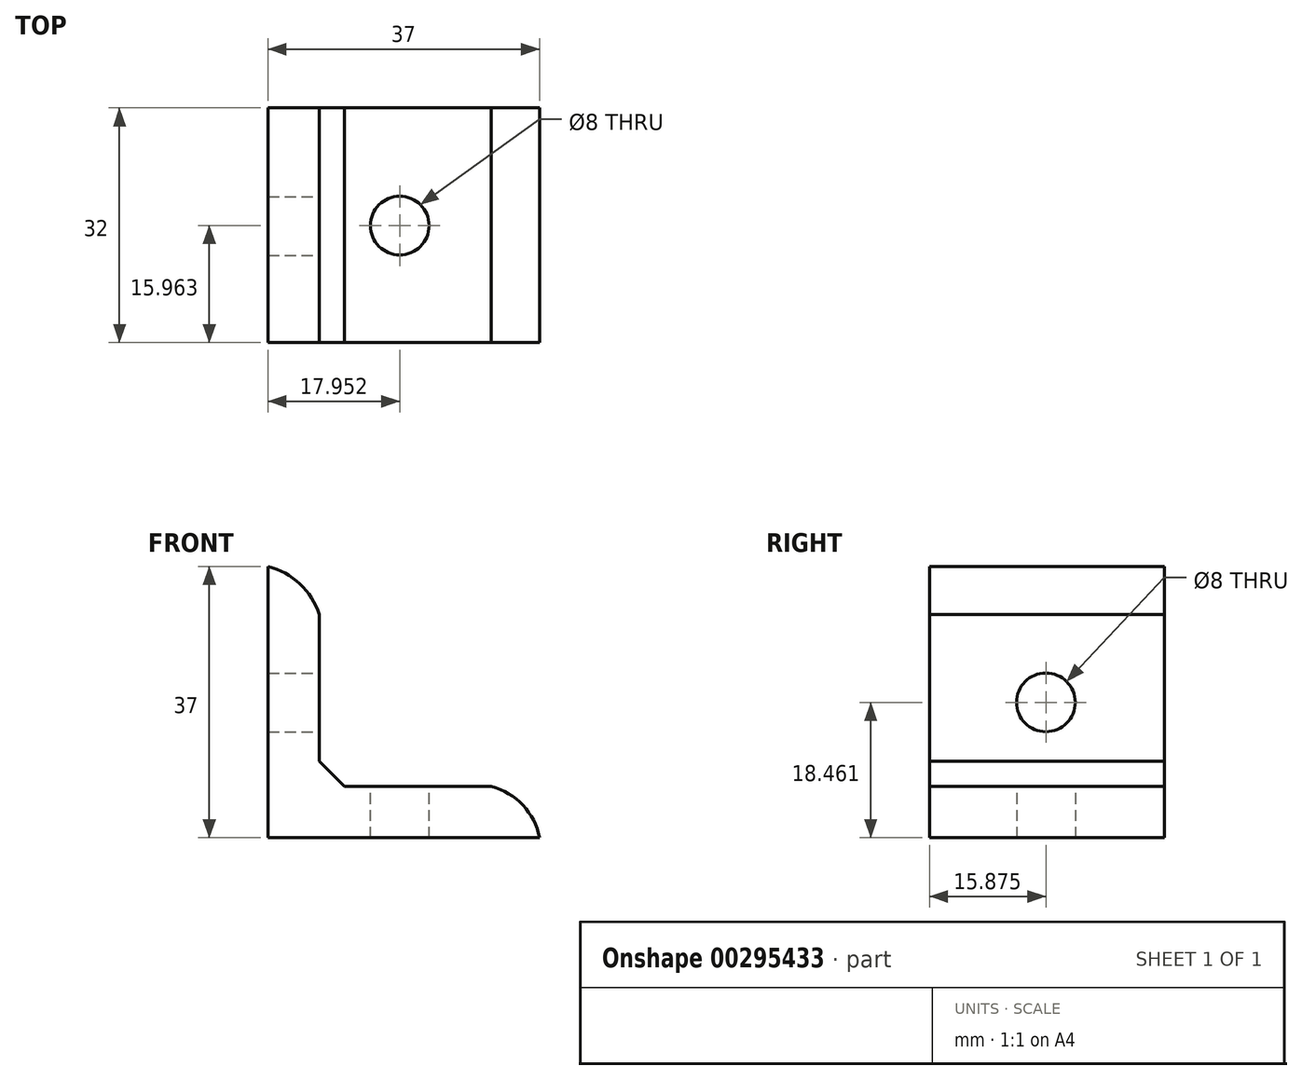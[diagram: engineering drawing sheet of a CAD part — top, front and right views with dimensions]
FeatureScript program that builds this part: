
annotation { "Feature Type Name" : "Feature", "Feature Type Description" : "" }
export const myFeature = defineFeature(function(context is Context, id is Id, definition is map)
    precondition{}
    {
        {
            var Q0;
            Q0=qCreatedBy(makeId("Front.planeOp"),FACE);
            var sketch = newSketch(context, id + "F0", { "sketchPlane" : qUnion([Q0])});
            skLineSegment(sketch, "E0", {"start": v(0, 0) * mm, "end": v(0, 37) * mm});
            skLineSegment(sketch, "E1", {"start": v(0, 0) * mm, "end": v(37, 0) * mm});
            skPoint(sketch, "E2", {"position": v(7, 30.44) * mm});
            skArc(sketch, "E3", {"start": v(7, 30.44) * mm, "mid": v(4.33, 34.6) * mm, "end": v(0, 37) * mm});
            skPoint(sketch, "E4", {"position": v(30.44, 7) * mm});
            skArc(sketch, "E5", {"start": v(37, 0) * mm, "mid": v(34.74, 4.45) * mm, "end": v(30.44, 7) * mm});
            skLineSegment(sketch, "E6", {"start": v(7, 30.44) * mm, "end": v(7, 10.44) * mm});
            skLineSegment(sketch, "E7", {"start": v(30.44, 7) * mm, "end": v(10.44, 7) * mm});
            skLineSegment(sketch, "E8", {"start": v(7, 10.44) * mm, "end": v(10.44, 7) * mm});
            skSolve(sketch);
        }
        {
            var Q0;
            Q0=makeQuery(id+"F0.imprint","IMPRINT",FACE,{"disambiguationData":[TD([[makeQuery(id+"F0.imprint","IMPRINT",EDGE,{"derivedFrom":sQuery(id+"F0.wireOp",EDGE,"E0")}),-1.0]])]});
            extrude(context, id + "F1", {"entities" : qUnion([Q0]), "depth" : 32 * mm});
        }
        {
            var Q0;
            Q0=makeQuery(id+"F1.opExtrude","SWEPT_FACE",FACE,{"disambiguationData":[OSD([sQuery(id+"F0.wireOp",EDGE,"E6")])]});
            var sketch = newSketch(context, id + "F2", { "sketchPlane" : qUnion([Q0])});
            skPoint(sketch, "E9", {"position": v(-20, 0) * mm});
            skCircle(sketch, "E10", {"center": v(-16.12, 18.46) * mm, "radius": 4 * mm});
            skSolve(sketch);
        }
        {
            var Q0;
            Q0=makeQuery(id+"F1.opExtrude","SWEPT_FACE",FACE,{"disambiguationData":[OSD([sQuery(id+"F0.wireOp",EDGE,"E7")])]});
            var sketch = newSketch(context, id + "F3", { "sketchPlane" : qUnion([Q0])});
            skPoint(sketch, "E11.endSnap0", {"position": v(30.44, -16) * mm});
            skCircle(sketch, "E12", {"center": v(17.95, -16.04) * mm, "radius": 3.85 * mm});
            skSolve(sketch);
        }
        {
            var Q0;
            Q0=sQuery(id+"F2.wireOp",VERTEX,"E10.center");
            var Q1;
            Q1=makeQuery(id+"F1.opExtrude","SWEPT_BODY",BODY,{"disambiguationData":[OSD([sQuery(id+"F0.wireOp",EDGE,"E0"),sQuery(id+"F0.wireOp",EDGE,"E1"),sQuery(id+"F0.wireOp",EDGE,"E3"),sQuery(id+"F0.wireOp",EDGE,"E5"),sQuery(id+"F0.wireOp",EDGE,"E6"),sQuery(id+"F0.wireOp",EDGE,"E7"),sQuery(id+"F0.wireOp",EDGE,"E8")])]});
            hole(context, id + "F4", {"style" : HoleStyle.SIMPLE, "endStyle" : HoleEndStyle.THROUGH, "holeDiameter" : 8 * mm, "tappedDepth" : 12 * mm, "tapClearance" : 3, "locations" : qUnion([Q0]), "scope" : qUnion([Q1])});
        }
        {
            var Q0;
            Q0=sQuery(id+"F3.wireOp",VERTEX,"E12.center");
            var Q1;
            Q1=makeQuery(id+"F1.opExtrude","SWEPT_BODY",BODY,{"disambiguationData":[OSD([sQuery(id+"F0.wireOp",EDGE,"E0"),sQuery(id+"F0.wireOp",EDGE,"E1"),sQuery(id+"F0.wireOp",EDGE,"E3"),sQuery(id+"F0.wireOp",EDGE,"E5"),sQuery(id+"F0.wireOp",EDGE,"E6"),sQuery(id+"F0.wireOp",EDGE,"E7"),sQuery(id+"F0.wireOp",EDGE,"E8")])]});
            hole(context, id + "F5", {"style" : HoleStyle.SIMPLE, "endStyle" : HoleEndStyle.THROUGH, "holeDiameter" : 8 * mm, "tappedDepth" : 12 * mm, "tapClearance" : 3, "locations" : qUnion([Q0]), "scope" : qUnion([Q1])});
        }
    });
